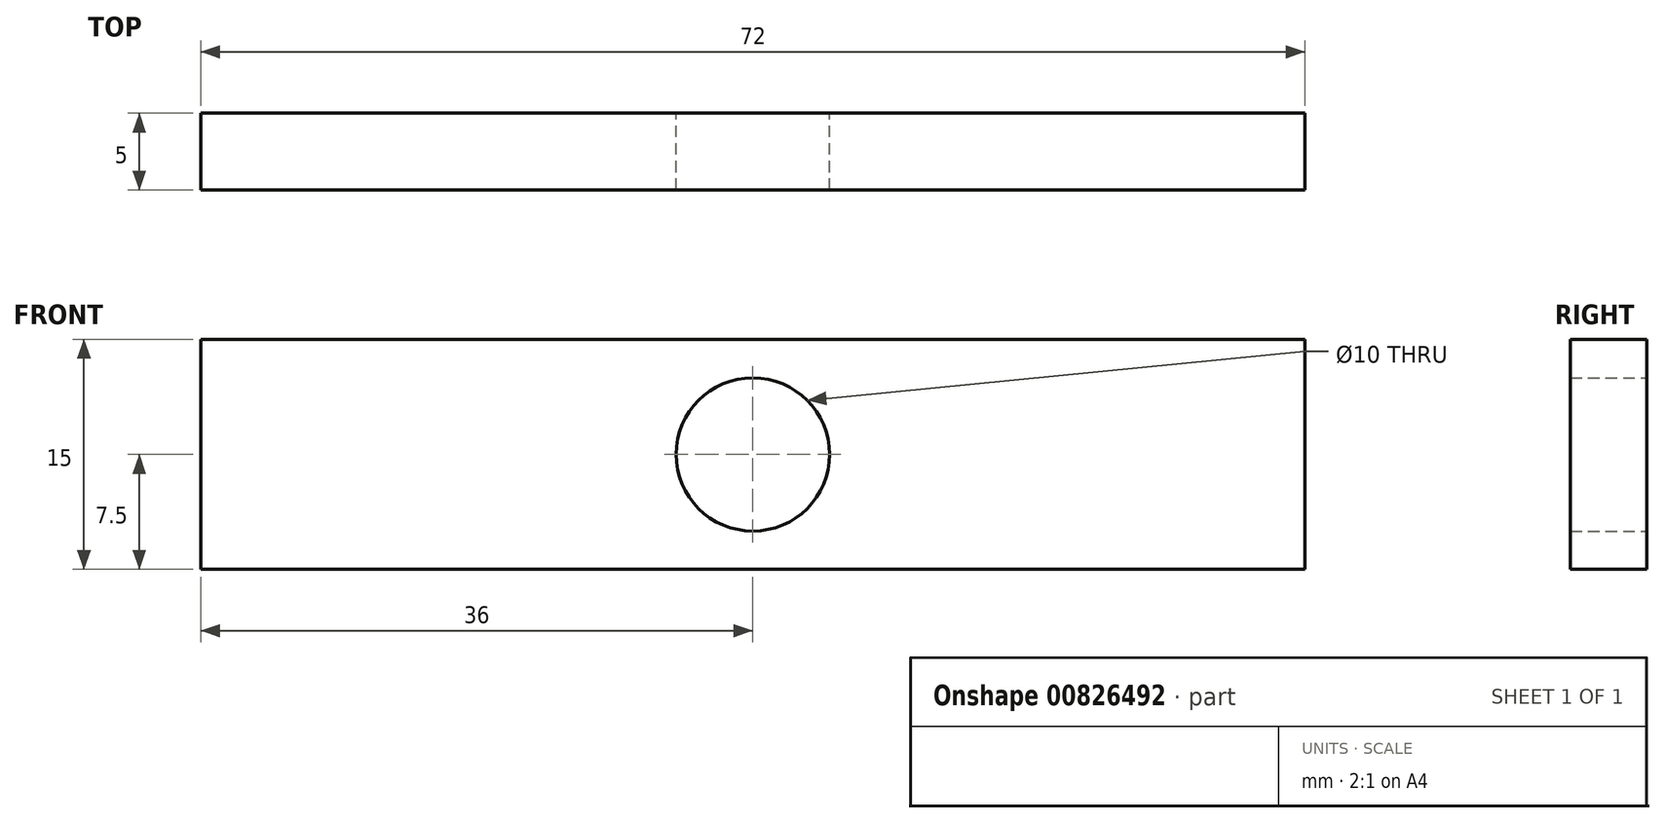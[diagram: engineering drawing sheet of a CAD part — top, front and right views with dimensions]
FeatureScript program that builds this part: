
annotation { "Feature Type Name" : "Feature", "Feature Type Description" : "" }
export const myFeature = defineFeature(function(context is Context, id is Id, definition is map)
    precondition{}
    {
        {
            var Q0;
            Q0=qCreatedBy(makeId("Front.planeOp"),FACE);
            var sketch = newSketch(context, id + "F0", { "sketchPlane" : qUnion([Q0])});
            skLineSegment(sketch, "E0.bottom", {"start": v(36, 7.5) * mm, "end": v(-36, 7.5) * mm});
            skLineSegment(sketch, "E0.top", {"start": v(36, -7.5) * mm, "end": v(-36, -7.5) * mm});
            skLineSegment(sketch, "E0.left", {"start": v(36, 7.5) * mm, "end": v(36, -7.5) * mm});
            skLineSegment(sketch, "E0.right", {"start": v(-36, 7.5) * mm, "end": v(-36, -7.5) * mm});
            skPoint(sketch, "E0.middle", {"position": v(0, 0) * mm});
            skCircle(sketch, "E1", {"center": v(0, 0) * mm, "radius": 5 * mm});
            skSolve(sketch);
        }
        {
            var Q0;
            Q0=makeQuery(id+"F0.imprint","IMPRINT",FACE,{"disambiguationData":[TD([[makeQuery(id+"F0.imprint","IMPRINT",EDGE,{"derivedFrom":sQuery(id+"F0.wireOp",EDGE,"E0.bottom")}),1.0]])]});
            extrude(context, id + "F1", {"entities" : qUnion([Q0]), "depth" : 5 * mm, "offsetDistance" : 25 * mm});
        }
    });
